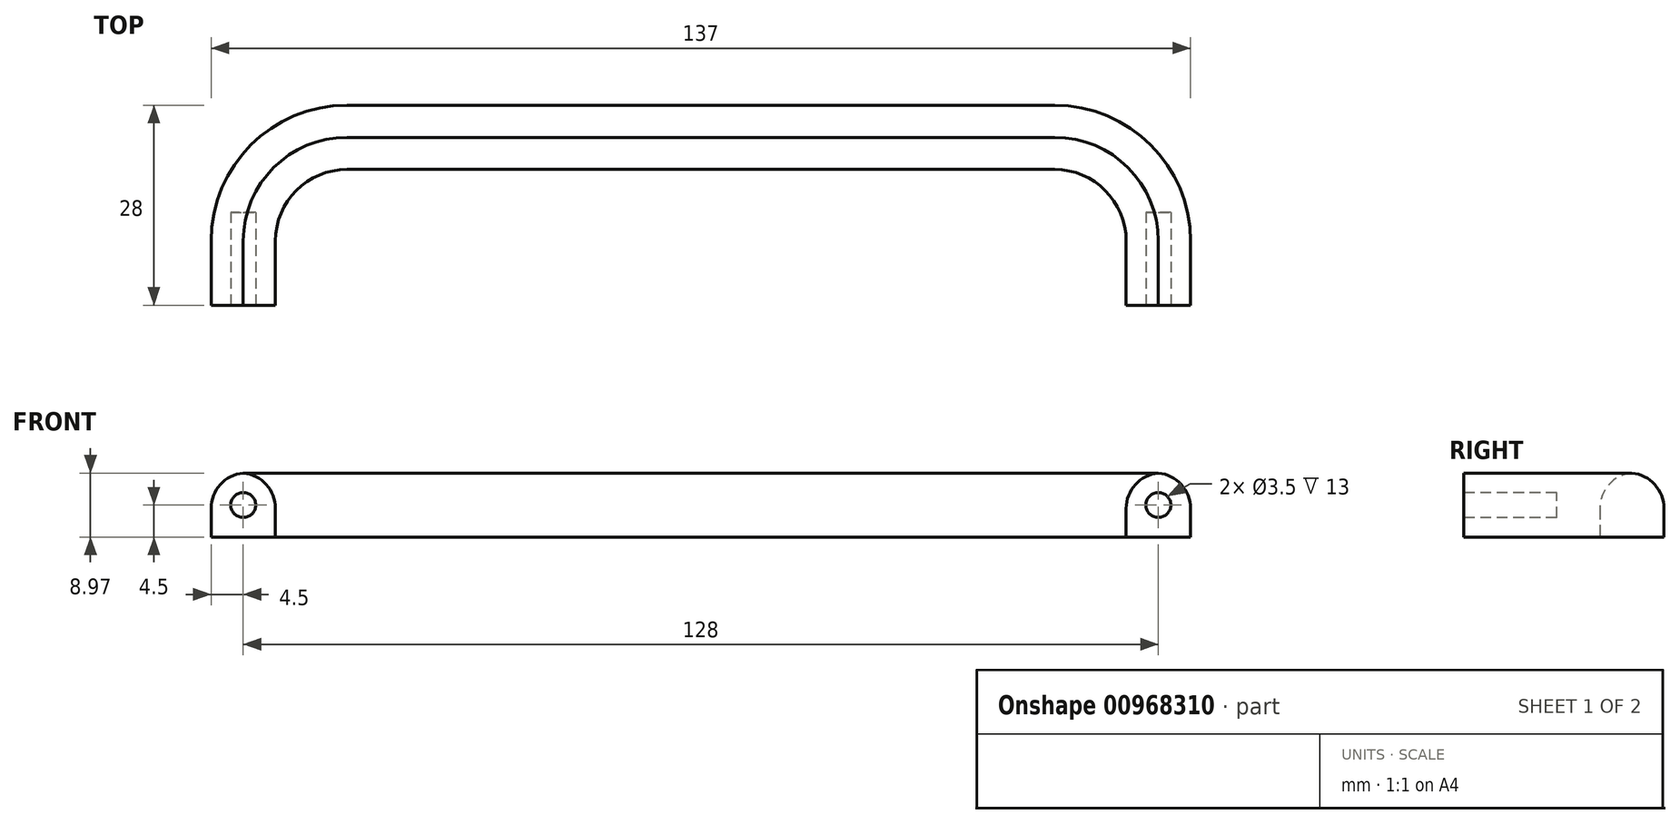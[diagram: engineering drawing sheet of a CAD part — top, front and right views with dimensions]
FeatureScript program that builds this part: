
annotation { "Feature Type Name" : "Feature", "Feature Type Description" : "" }
export const myFeature = defineFeature(function(context is Context, id is Id, definition is map)
    precondition{}
    {
        {
            var Q0;
            Q0=qCreatedBy(makeId("Top.planeOp"),FACE);
            var sketch = newSketch(context, id + "F0", { "sketchPlane" : qUnion([Q0])});
            skLineSegment(sketch, "E0", {"start": v(0, 0) * mm, "end": v(0, 9) * mm});
            skLineSegment(sketch, "E1", {"start": v(19, 28) * mm, "end": v(118, 28) * mm});
            skLineSegment(sketch, "E2", {"start": v(137, 9) * mm, "end": v(137, 0) * mm});
            skLineSegment(sketch, "E3", {"start": v(137, 0) * mm, "end": v(128, 0) * mm});
            skLineSegment(sketch, "E4", {"start": v(128, 0) * mm, "end": v(128, 9) * mm});
            skLineSegment(sketch, "E5", {"start": v(118, 19) * mm, "end": v(19, 19) * mm});
            skLineSegment(sketch, "E6", {"start": v(9, 9) * mm, "end": v(9, 0) * mm});
            skLineSegment(sketch, "E7", {"start": v(9, 0) * mm, "end": v(0, 0) * mm});
            skPoint(sketch, "E8.visualSharp", {"position": v(9, 19) * mm});
            skArc(sketch, "E8.filletArc", {"start": v(19, 19) * mm, "mid": v(11.93, 16.07) * mm, "end": v(9, 9) * mm});
            skPoint(sketch, "E9.visualSharp", {"position": v(128, 19) * mm});
            skArc(sketch, "E9.filletArc", {"start": v(128, 9) * mm, "mid": v(125.07, 16.07) * mm, "end": v(118, 19) * mm});
            skPoint(sketch, "E10.visualSharp", {"position": v(0, 28) * mm});
            skPoint(sketch, "E11.visualSharp", {"position": v(137, 28) * mm});
            skArc(sketch, "E12.filletArc", {"start": v(19, 28) * mm, "mid": v(5.56, 22.44) * mm, "end": v(0, 9) * mm});
            skArc(sketch, "E13.filletArc", {"start": v(137, 9) * mm, "mid": v(131.44, 22.44) * mm, "end": v(118, 28) * mm});
            skSolve(sketch);
        }
        {
            var Q0;
            Q0=makeQuery(id+"F0.imprint","IMPRINT",FACE,{"disambiguationData":[TD([[makeQuery(id+"F0.imprint","IMPRINT",EDGE,{"derivedFrom":sQuery(id+"F0.wireOp",EDGE,"E0")}),-1.0]])]});
            extrude(context, id + "F1", {"entities" : qUnion([Q0]), "depth" : 9 * mm, "offsetDistance" : 25 * mm});
        }
        {
            var Q0;
            Q0=makeQuery(id+"F1.opExtrude","CAP_EDGE",EDGE,{"disambiguationData":[OSD([sQuery(id+"F0.wireOp",EDGE,"E0")])],"isStart":false});
            var Q1;
            Q1=makeQuery(id+"F1.opExtrude","CAP_EDGE",EDGE,{"disambiguationData":[OSD([sQuery(id+"F0.wireOp",EDGE,"E12.filletArc")])],"isStart":false});
            var Q2;
            Q2=makeQuery(id+"F1.opExtrude","CAP_EDGE",EDGE,{"disambiguationData":[OSD([sQuery(id+"F0.wireOp",EDGE,"E1")])],"isStart":false});
            var Q3;
            Q3=makeQuery(id+"F1.opExtrude","CAP_EDGE",EDGE,{"disambiguationData":[OSD([sQuery(id+"F0.wireOp",EDGE,"E13.filletArc")])],"isStart":false});
            var Q4;
            Q4=makeQuery(id+"F1.opExtrude","CAP_EDGE",EDGE,{"disambiguationData":[OSD([sQuery(id+"F0.wireOp",EDGE,"E2")])],"isStart":false});
            var Q5;
            Q5=makeQuery(id+"F1.opExtrude","CAP_EDGE",EDGE,{"disambiguationData":[OSD([sQuery(id+"F0.wireOp",EDGE,"E4")])],"isStart":false});
            var Q6;
            Q6=makeQuery(id+"F1.opExtrude","CAP_EDGE",EDGE,{"disambiguationData":[OSD([sQuery(id+"F0.wireOp",EDGE,"E9.filletArc")])],"isStart":false});
            fillet(context, id + "F2", {"entities" : qUnion([Q0, Q1, Q2, Q3, Q4, Q5, Q6]), "radius" : 5 * mm, "tangentPropagation" : true, "allowEdgeOverflow" : false});
        }
        {
            var Q0;
            Q0=makeQuery(id+"F1.opExtrude","SWEPT_FACE",FACE,{"disambiguationData":[OSD([sQuery(id+"F0.wireOp",EDGE,"E7")])]});
            var sketch = newSketch(context, id + "F3", { "sketchPlane" : qUnion([Q0])});
            skCircle(sketch, "E14", {"center": v(4.5, 4.5) * mm, "radius": 1.75 * mm});
            skPoint(sketch, "E14.centerSnap0", {"position": v(4.5, 0) * mm});
            skCircle(sketch, "E15", {"center": v(132.5, 4.5) * mm, "radius": 1.75 * mm});
            skSolve(sketch);
        }
        {
            var Q0;
            Q0 = qSketchRegion(id + "F3", true);
            extrude(context, id + "F4", {"entities" : qUnion([Q0]), "operationType" : NewBodyOperationType.REMOVE, "oppositeDirection" : true, "depth" : 13 * mm, "offsetDistance" : 25 * mm});
        }
    });
